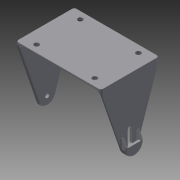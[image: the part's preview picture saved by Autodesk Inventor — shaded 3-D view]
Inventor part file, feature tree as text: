
AUTODESK INVENTOR PART (.ipt)
format: ipt  version: 2015 SP1 (Build 190203100, 203)  size: 297,984 bytes
history: native  units: mm
features: sketch x8, extrude x8, projected_geometry x4, fillet x3, mirror x2, hole x1
ambient origin geometry x8: Origin, YZ Plane, XZ Plane, XY Plane, X Axis, Y Axis, Z Axis, Center Point
bodies: Solid1 (feature_tree)
feature tree (26):
  sketch  "Sketch1"  dims[d0=70.0mm d1=50.8mm]
  extrude  "Extrusion1"  Depth=50.8mm
  hole  "Hole1"  [1 undecoded]
  extrude  "Extrusion2"  Depth=2.0mm TaperAngle=0.0deg
  mirror  "Mirror1"
  extrude  "Extrusion3"  Depth=15.0mm
  extrude  "Extrusion4"  Depth=2.0mm
  fillet  "Fillet3"  Radius=2.0mm
  extrude  "Extrusion5"  Depth=2.0mm TaperAngle=0.0deg
  extrude  "Extrusion6"  TaperAngle=60.0deg  [1 undecoded]
  extrude  "Extrusion7"  Depth=50.8mm
  extrude  "Extrusion8"  Depth=38.1mm
  mirror  "Mirror2"
  fillet  "Fillet1"  Radius=2.0mm
  fillet  "Fillet2"  Radius=1.0mm
  sketch  "Sketch2"  dims[d2=2.0mm d3=0.0mm d4=50.8mm]
  projected_geometry  "Projected Loop1"
  sketch  "Sketch3"  dims[d5=7.62mm d7=2.0mm d8=0.0mm]
  sketch  "Sketch4"  dims[d9=3.75mm d10=15.0mm]
  sketch  "Sketch5"  dims[d11=2.0mm d12=0.0mm d13=2.0mm d14=2.0mm d15=0.0mm]
  projected_geometry  "Projected Loop2"
  sketch  "Sketch6"  dims[d16=2.0mm d17=0.0mm d18=2.0mm d19=0.0mm]
  sketch  "Sketch7"  dims[d20=1.0mm d21=0.0mm d22=60.0deg]
  projected_geometry  "Projected Loop3"
  sketch  "Sketch8"  dims[d23=1.0mm d24=0.0mm d25=50.8mm d26=38.1mm d27=4.305mm d28=6.0mm d29=7.087mm d30=2.0mm d31=14.3117mm d32=8.0mm d33=20.594885mm d34=2.0mm d35=1.0mm d36=3.0mm d37=5.62mm]
  projected_geometry  "Projected Loop4"
note: 2 required parameter values undecoded (feature->parameter linkage not recoverable at this tier; creation-order binding heuristic only, values carry confidence <= 0.55)
